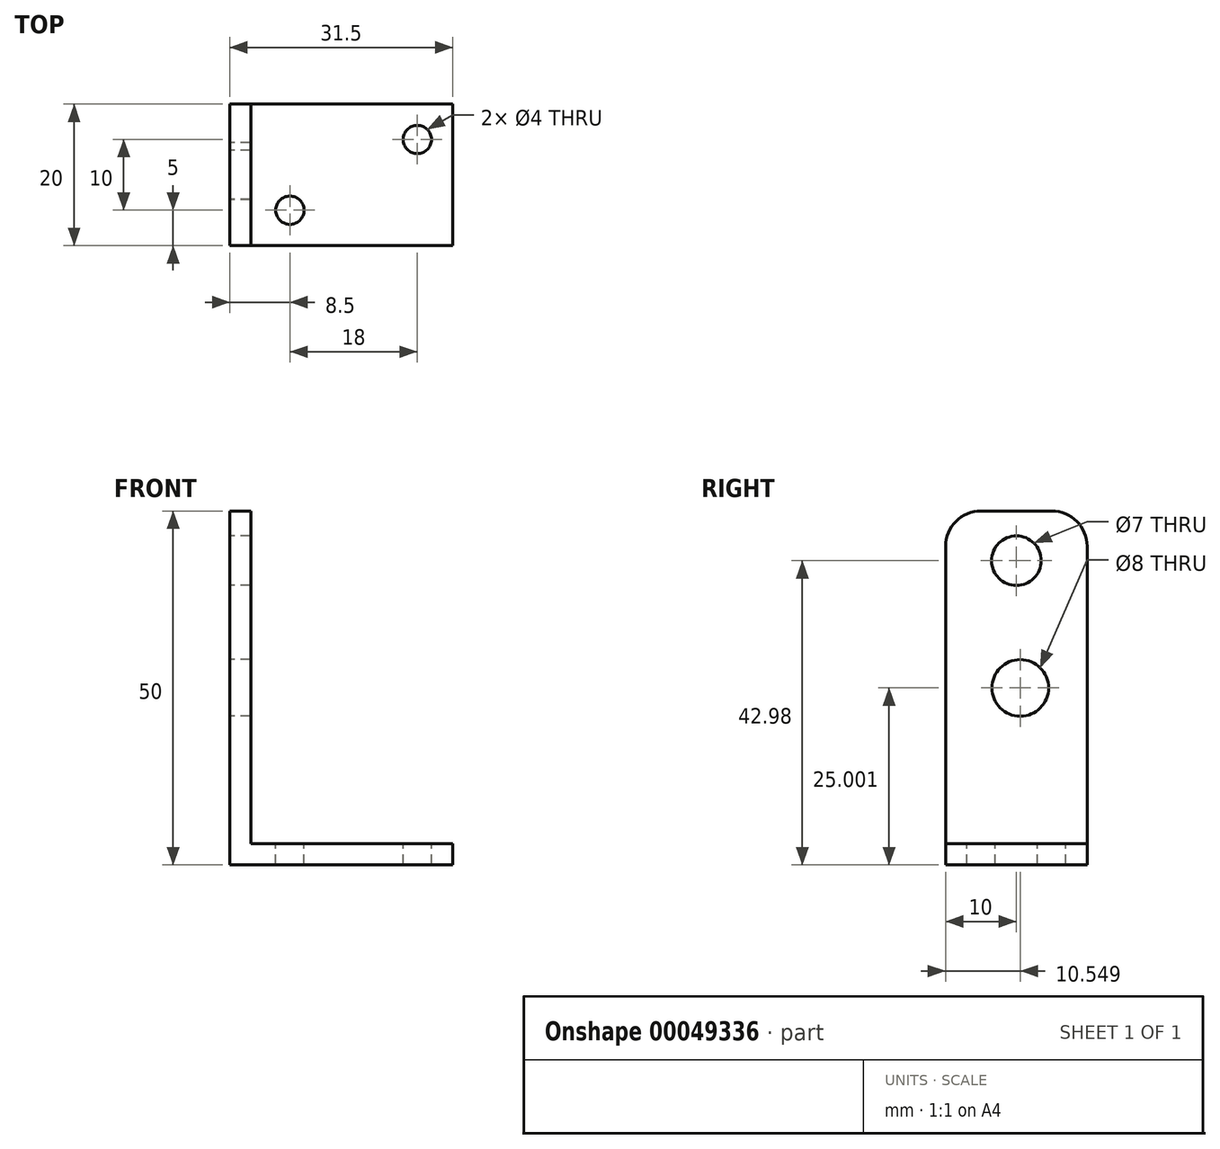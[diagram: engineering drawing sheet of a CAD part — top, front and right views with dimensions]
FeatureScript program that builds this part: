
annotation { "Feature Type Name" : "Feature", "Feature Type Description" : "" }
export const myFeature = defineFeature(function(context is Context, id is Id, definition is map)
    precondition{}
    {
        {
            var Q0;
            Q0=qCreatedBy(makeId("Right.planeOp"),FACE);
            var sketch = newSketch(context, id + "F0", { "sketchPlane" : qUnion([Q0])});
            skCircle(sketch, "E0", {"center": v(0, 0) * mm, "radius": 3.5 * mm});
            skLineSegment(sketch, "E1", {"start": v(-10, -42.98) * mm, "end": v(10, -42.98) * mm});
            skLineSegment(sketch, "E2", {"start": v(0, 12.72) * mm, "end": v(0, -46.69) * mm, "construction": true});
            skLineSegment(sketch, "E3", {"start": v(-10, 2.02) * mm, "end": v(-10, -42.98) * mm});
            skLineSegment(sketch, "E4", {"start": v(-5, 7.02) * mm, "end": v(5, 7.02) * mm});
            skLineSegment(sketch, "E5", {"start": v(10, 2.02) * mm, "end": v(10, -42.98) * mm});
            skCircle(sketch, "E6", {"center": v(0.55, -17.98) * mm, "radius": 4 * mm});
            skPoint(sketch, "E7.visualSharp", {"position": v(-10, 7.02) * mm});
            skArc(sketch, "E7.filletArc", {"start": v(-5, 7.02) * mm, "mid": v(-8.54, 5.56) * mm, "end": v(-10, 2.02) * mm});
            skPoint(sketch, "E8.visualSharp", {"position": v(10, 7.02) * mm});
            skArc(sketch, "E8.filletArc", {"start": v(10, 2.02) * mm, "mid": v(8.54, 5.56) * mm, "end": v(5, 7.02) * mm});
            skLineSegment(sketch, "E9", {"start": v(-10, -39.98) * mm, "end": v(10, -39.98) * mm});
            skSolve(sketch);
        }
        {
            var Q0;
            {var subQ2=sQuery(id+"F0.wireOp",EDGE,"E1");Q0=makeQuery(id+"F0.imprint","IMPRINT",FACE,{"disambiguationData":[TD([[makeQuery(id+"F0.imprint","IMPRINT",EDGE,{"derivedFrom":subQ2}),1.0]])]});}
            extrude(context, id + "F1", {"entities" : qUnion([Q0]), "depth" : 31.5 * mm});
        }
        {
            var Q0;
            Q0=qSketchRegion(id+"F0",true);
            extrude(context, id + "F2", {"entities" : qUnion([Q0]), "operationType" : NewBodyOperationType.ADD, "depth" : 3 * mm});
        }
        {
            var Q0;
            Q0=qCreatedBy(makeId("Top.planeOp"),FACE);
            var sketch = newSketch(context, id + "F3", { "sketchPlane" : qUnion([Q0])});
            skCircle(sketch, "E10", {"center": v(26.5, 5) * mm, "radius": 2 * mm});
            skCircle(sketch, "E11", {"center": v(8.5, -5) * mm, "radius": 2 * mm});
            skSolve(sketch);
        }
        {
            var Q0;
            Q0=makeQuery(id+"F3.imprint","IMPRINT",FACE,{"disambiguationData":[TD([[makeQuery(id+"F3.imprint","IMPRINT",EDGE,{"derivedFrom":sQuery(id+"F3.wireOp",EDGE,"E10")}),1.0]])]});
            var Q1;
            Q1=makeQuery(id+"F3.imprint","IMPRINT",FACE,{"disambiguationData":[TD([[makeQuery(id+"F3.imprint","IMPRINT",EDGE,{"derivedFrom":sQuery(id+"F3.wireOp",EDGE,"E11")}),1.0]])]});
            extrude(context, id + "F4", {"entities" : qUnion([Q0, Q1]), "operationType" : NewBodyOperationType.REMOVE, "oppositeDirection" : true, "depth" : 55.92 * mm});
        }
    });
